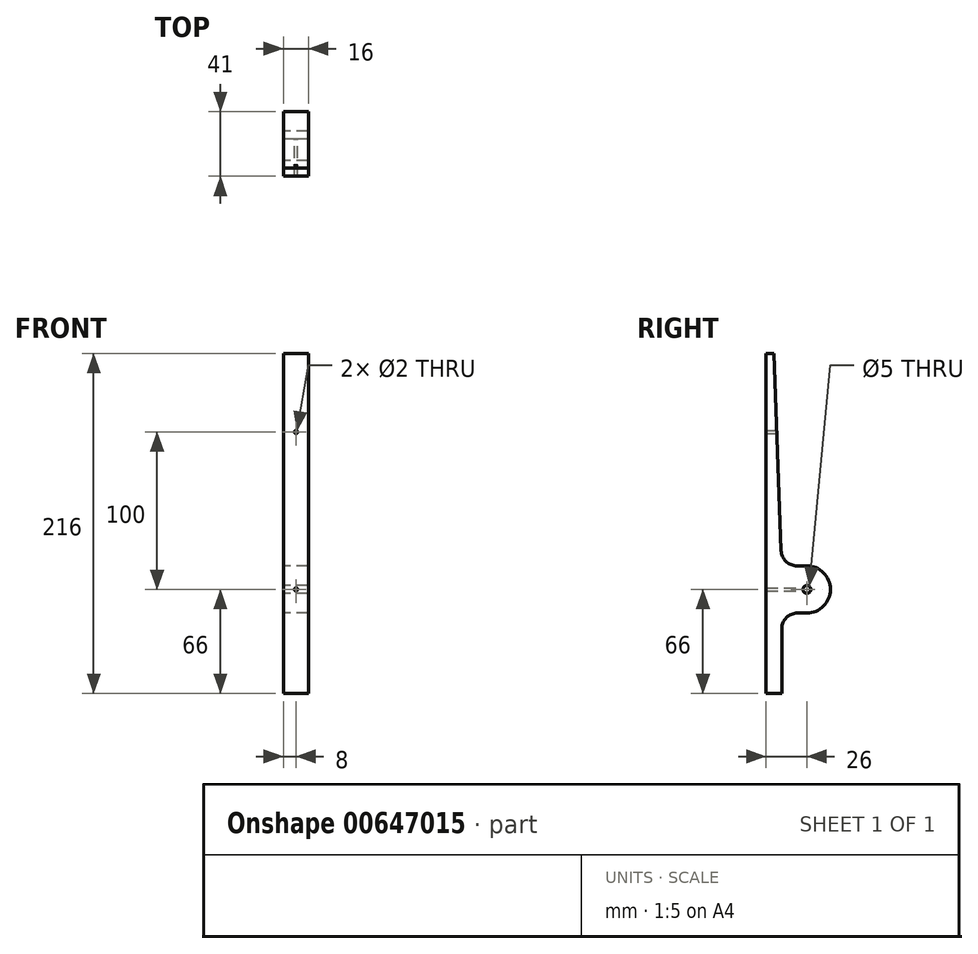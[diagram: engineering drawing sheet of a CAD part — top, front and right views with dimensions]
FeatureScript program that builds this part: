
annotation { "Feature Type Name" : "Feature", "Feature Type Description" : "" }
export const myFeature = defineFeature(function(context is Context, id is Id, definition is map)
    precondition{}
    {
        {
            var Q0;
            Q0=qCreatedBy(makeId("Right.planeOp"),FACE);
            var sketch = newSketch(context, id + "F0", { "sketchPlane" : qUnion([Q0])});
            skLineSegment(sketch, "E0", {"start": v(0, 0) * mm, "end": v(-16, 0) * mm, "construction": true});
            skLineSegment(sketch, "E1", {"start": v(-16, 0) * mm, "end": v(-16, -66) * mm, "construction": true});
            skLineSegment(sketch, "E2.bottom", {"start": v(-16, -66) * mm, "end": v(-26, -66) * mm});
            skLineSegment(sketch, "E2.top", {"start": v(-21, 150) * mm, "end": v(-26, 150) * mm});
            skLineSegment(sketch, "E2.left", {"start": v(-16, -66) * mm, "end": v(-16, -25) * mm});
            skLineSegment(sketch, "E2.right", {"start": v(-26, -66) * mm, "end": v(-26, 150) * mm});
            skLineSegment(sketch, "E3.top", {"start": v(-6.36, 15) * mm, "end": v(0, 15) * mm});
            skLineSegment(sketch, "E4.trimOffspring", {"start": v(-6, -15) * mm, "end": v(0, -15) * mm});
            skLineSegment(sketch, "E5.trimOffspring", {"start": v(-16, 15) * mm, "end": v(-16, 150) * mm, "construction": true});
            skArc(sketch, "E6", {"start": v(0, 15) * mm, "mid": v(15, 0) * mm, "end": v(0, -15) * mm});
            skLineSegment(sketch, "E7", {"start": v(-16.36, 24.63) * mm, "end": v(-21, 150) * mm});
            skPoint(sketch, "E8.visualSharp", {"position": v(-16, 15) * mm});
            skArc(sketch, "E8.filletArc", {"start": v(-16.36, 24.63) * mm, "mid": v(-13.3, 17.8) * mm, "end": v(-6.36, 15) * mm});
            skPoint(sketch, "E9.visualSharp", {"position": v(-16, -15) * mm});
            skArc(sketch, "E9.filletArc", {"start": v(-6, -15) * mm, "mid": v(-13.07, -17.93) * mm, "end": v(-16, -25) * mm});
            skCircle(sketch, "E10", {"center": v(0, 0) * mm, "radius": 2.5 * mm});
            skSolve(sketch);
        }
        {
            var Q0;
            Q0 = qSketchRegion(id + "F0", true);
            extrude(context, id + "F1", {"entities" : qUnion([Q0]), "endBound" : BoundingType.SYMMETRIC, "depth" : 16 * mm, "offsetDistance" : 25 * mm});
        }
        {
            var Q0;
            Q0=qCreatedBy(makeId("Front.planeOp"),FACE);
            var sketch = newSketch(context, id + "F2", { "sketchPlane" : qUnion([Q0])});
            skCircle(sketch, "E11", {"center": v(0, -75) * mm, "radius": 1 * mm});
            skCircle(sketch, "E12", {"center": v(0, 0) * mm, "radius": 1 * mm});
            skCircle(sketch, "E13", {"center": v(0, 100) * mm, "radius": 1 * mm});
            skSolve(sketch);
        }
        {
            var Q0;
            Q0 = qSketchRegion(id + "F2", true);
            extrude(context, id + "F3", {"entities" : qUnion([Q0]), "operationType" : NewBodyOperationType.REMOVE, "endBound" : BoundingType.THROUGH_ALL, "depth" : 25 * mm, "offsetDistance" : 25 * mm});
        }
    });
